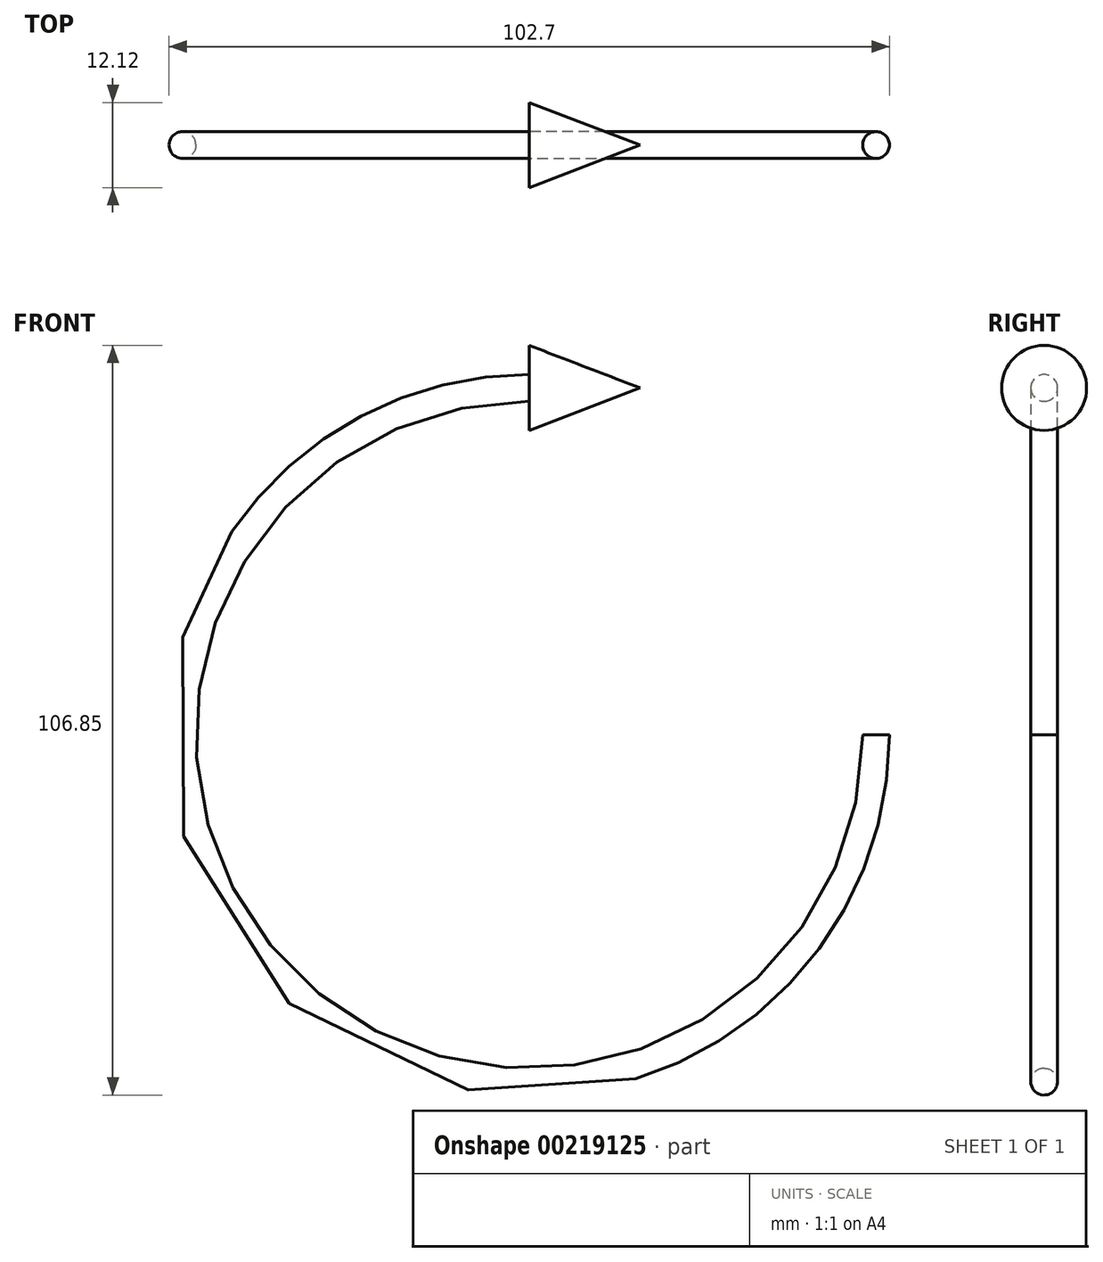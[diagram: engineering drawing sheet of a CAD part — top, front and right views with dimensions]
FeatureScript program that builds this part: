
annotation { "Feature Type Name" : "Feature", "Feature Type Description" : "" }
export const myFeature = defineFeature(function(context is Context, id is Id, definition is map)
    precondition{}
    {
        {
            var Q0;
            Q0=qCreatedBy(makeId("Right.planeOp"),FACE);
            var sketch = newSketch(context, id + "F0", { "sketchPlane" : qUnion([Q0])});
            skCircle(sketch, "E0", {"center": v(0, 49.44) * mm, "radius": 1.9 * mm});
            skLineSegment(sketch, "E1", {"start": v(25.23, 0) * mm, "end": v(-21.7, 0) * mm, "construction": true});
            skSolve(sketch);
        }
        {
            var Q0;
            Q0 = qSketchRegion(id + "F0", true);
            var Q1;
            Q1=sQuery(id+"F0.wireOp",EDGE,"E1");
            revolve(context, id + "F1", {"entities" : qUnion([Q0]), "axis" : qUnion([Q1]), "revolveType" : RevolveType.ONE_DIRECTION, "angle" : 270 * degree});
        }
        {
            var Q0;
            Q0=qCreatedBy(makeId("Front.planeOp"),FACE);
            var sketch = newSketch(context, id + "F2", { "sketchPlane" : qUnion([Q0])});
            skLineSegment(sketch, "E2", {"start": v(0, 49.44) * mm, "end": v(15.8, 49.44) * mm});
            skLineSegment(sketch, "E3", {"start": v(0, 49.44) * mm, "end": v(0, 55.5) * mm});
            skLineSegment(sketch, "E4", {"start": v(0, 55.5) * mm, "end": v(15.8, 49.44) * mm});
            skSolve(sketch);
        }
        {
            var Q0;
            Q0 = qSketchRegion(id + "F2", true);
            var Q1;
            Q1=sQuery(id+"F2.wireOp",EDGE,"E2");
            revolve(context, id + "F3", {"entities" : qUnion([Q0]), "axis" : qUnion([Q1]), "revolveType" : RevolveType.FULL});
        }
    });
